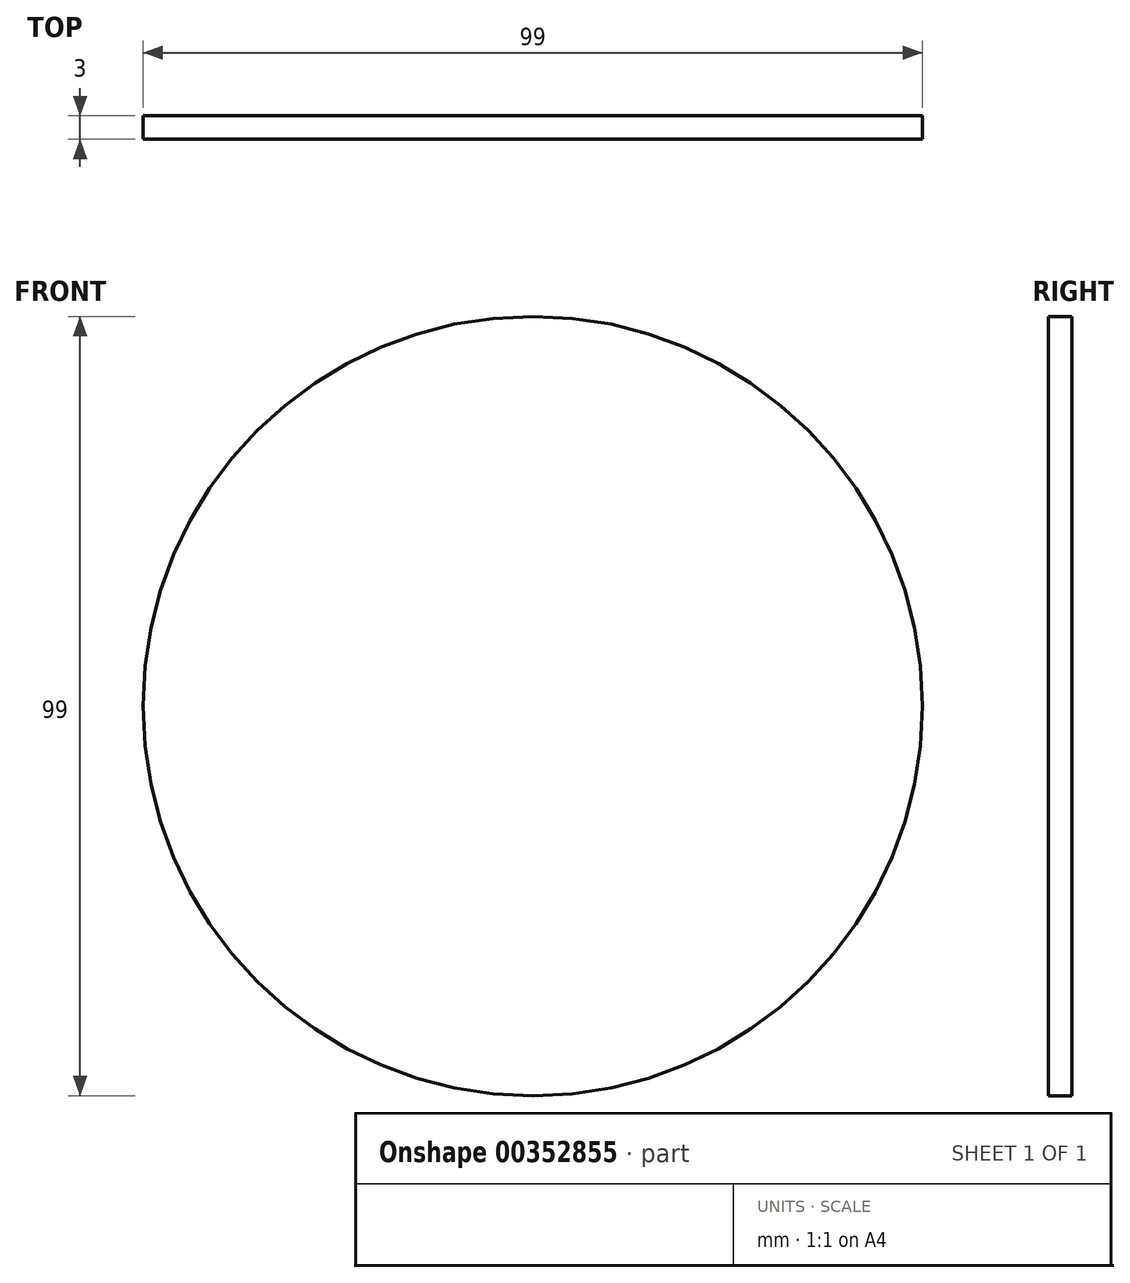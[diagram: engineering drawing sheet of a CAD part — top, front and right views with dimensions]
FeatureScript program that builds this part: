
annotation { "Feature Type Name" : "Feature", "Feature Type Description" : "" }
export const myFeature = defineFeature(function(context is Context, id is Id, definition is map)
    precondition{}
    {
        {
            var Q0;
            Q0=qCreatedBy(makeId("Front.planeOp"),FACE);
            var sketch = newSketch(context, id + "F0", { "sketchPlane" : qUnion([Q0])});
            skCircle(sketch, "E0", {"center": v(0, 0) * mm, "radius": 49.5 * mm});
            skSolve(sketch);
        }
        {
            var Q0;
            Q0 = qSketchRegion(id + "F0", true);
            extrude(context, id + "F1", {"entities" : qUnion([Q0]), "depth" : 3 * mm});
        }
    });
